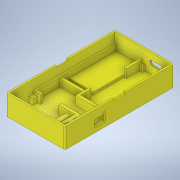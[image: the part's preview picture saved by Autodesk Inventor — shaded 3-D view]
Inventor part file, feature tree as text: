
AUTODESK INVENTOR PART (.ipt)
format: ipt  version: 2020.1 (Build 241239000, 239)  size: 788,992 bytes
history: native  units: mm
features: extrude x18, sketch x13, chamfer x4, plane x2, fillet x2, emboss x2
ambient origin geometry x8: Origin, YZ Plane, XZ Plane, XY Plane, X Axis, Y Axis, Z Axis, Center Point
bodies: Solid1 (feature_tree)
feature tree (41):
  sketch  "Sketch1"  dims[d4=1.2mm d7=1.0mm]
  extrude  "Extrusion1"  Depth=1.0mm
  extrude  "Extrusion2"  Depth=13.0mm TaperAngle=0.0deg
  plane  "Work Plane1"
  sketch  "Sketch3"  dims[d8=1.2mm d9=0.0mm d10=13.0mm d11=0.0mm]
  extrude  "Extrusion6"  Depth=3.5mm
  extrude  "Extrusion5"  Depth=4.0mm
  extrude  "Extrusion7"  Depth=16.8mm
  extrude  "Extrusion8"  Depth=1.2mm
  extrude  "Extrusion9"  Depth=1.5mm
  fillet  "Fillet1"  Radius=1.5mm
  chamfer  "Chamfer2"  Distance=3.5mm
  extrude  "Extrusion10"  Depth=2.4mm
  extrude  "Extrusion11"  Depth=1.4mm
  chamfer  "Chamfer1"  Distance=1.38mm
  plane  "Work Plane2"
  extrude  "Extrusion14"  Depth=10.0mm
  extrude  "Extrusion15"  Depth=1.0mm TaperAngle=0.0deg
  extrude  "Extrusion16"  Depth=25.0mm
  extrude  "Extrusion17"  Depth=2.0mm TaperAngle=0.0deg
  chamfer  "Chamfer4"  Distance=2.2mm
  chamfer  "Chamfer5"  Distance=5.1mm
  extrude  "Extrusion21"  Depth=2.0mm TaperAngle=0.0deg
  extrude  "Extrusion22"  Depth=2.0mm TaperAngle=0.0deg
  emboss  "Emboss2"
  extrude  "Extrusion23"  Depth=0.5mm
  fillet  "Fillet3"  Radius=0.3mm
  extrude  "Extrusion24"  Depth=2.0mm TaperAngle=0.0deg
  emboss  "Emboss3"
  extrude  "Extrusion25"  Depth=1.0mm TaperAngle=45.0deg
  sketch  "Sketch4"  dims[d20=18.3mm d21=43.8mm d22=29.25mm d23=15.5mm d28=1.2mm d29=3.5mm]
  sketch  "Sketch5"  dims[d33=6.5mm d35=4.0mm]
  sketch  "Sketch6"  dims[d37=8.0mm d38=16.8mm]
  sketch  "Sketch7"  dims[d39=56.0mm d42=1.2mm]
  sketch  "Sketch12"  dims[d46=1.2mm d47=0.0mm d48=38.2mm d49=1.5mm]
  sketch  "Sketch13"  dims[d50=1.2mm]
  sketch  "Sketch16"  dims[d51=1.5mm]
  sketch  "Sketch17"  dims[d52=4.0mm]
  sketch  "Sketch18"  dims[d60=3.0mm]
  sketch  "Sketch19"  dims[d61=3.0mm]
  sketch  "Sketch20"  dims[d62=3.0mm d73=3.5mm d74=2.4mm d75=1.4mm d76=1.38mm d77=1.28mm d81=1.0mm d82=0.0mm d83=25.0mm d84=2.0mm d85=0.0mm d86=2.2mm d87=0.0mm d88=5.1mm d89=2.0mm d90=0.0mm d91=2.0mm d92=0.0mm d93=0.5mm d94=0.3mm d95=0.0mm d96=2.0mm d97=0.0mm d98=1.0mm d99=2.0mm d100=45.0deg d103=0.5mm d104=2.0mm d105=45.0deg d109=7.9mm d110=3.0mm d111=0.0mm d113=8.0mm d114=1.0mm d115=3.0mm d116=0.0mm d118=3.0mm d119=0.0mm d120=13.5mm d121=3.1mm d122=3.0mm d123=3.0mm d124=0.0mm d135=0.5mm d136=2.0mm d137=45.0deg d145=0.1mm d146=2.0mm d147=45.0deg d154=2.0mm d155=2.0mm d156=2.0mm d157=2.0mm d162=33.5mm d163=2.0mm d164=0.0mm d166=2.0mm d167=5.0mm d168=0.0mm d169=38.0mm d170=0.2mm d171=0.0mm d172=3.0mm d173=3.0mm d191=0.4mm d192=2.2mm d193=1.0mm d194=1.0mm d195=2.0mm d196=0.0mm d197=1.1mm d198=3.0mm d199=8.0mm d200=22.5deg d201=45.0deg d202=1.6mm d203=10.0mm d204=0.0mm d205=7.62mm d206=2.54mm d207=0.5mm d208=0.0mm d209=1.3mm d210=10.0mm d211=0.0mm]
